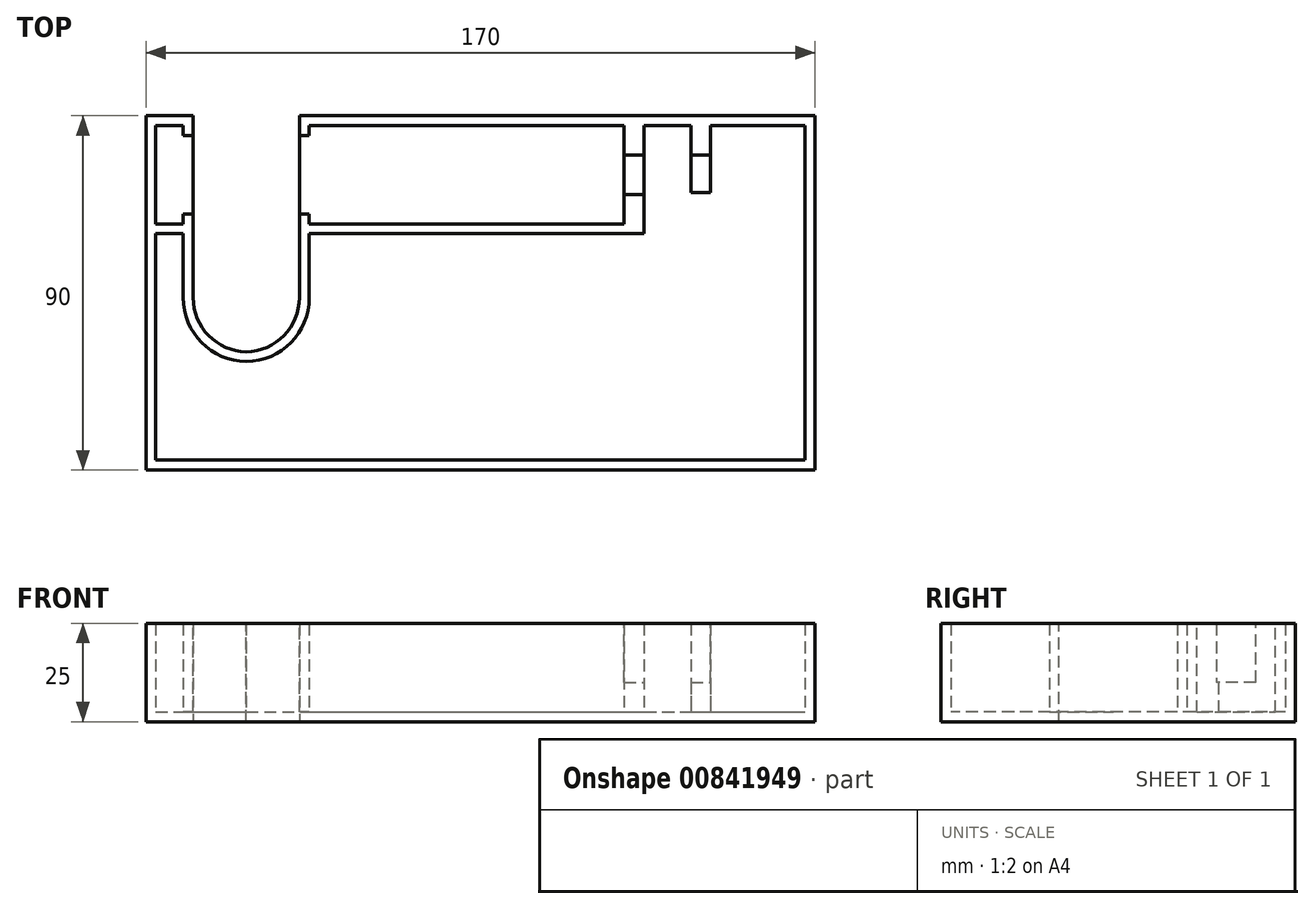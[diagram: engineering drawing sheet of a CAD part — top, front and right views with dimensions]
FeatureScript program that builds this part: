
annotation { "Feature Type Name" : "Feature", "Feature Type Description" : "" }
export const myFeature = defineFeature(function(context is Context, id is Id, definition is map)
    precondition{}
    {
        {
            var Q0;
            Q0=qCreatedBy(makeId("Top.planeOp"),FACE);
            var sketch = newSketch(context, id + "F0", { "sketchPlane" : qUnion([Q0])});
            skLineSegment(sketch, "E0.bottom", {"start": v(-85, 45) * mm, "end": v(85, 45) * mm});
            skLineSegment(sketch, "E0.top", {"start": v(-85, -45) * mm, "end": v(85, -45) * mm});
            skLineSegment(sketch, "E0.left", {"start": v(-85, 45) * mm, "end": v(-85, -45) * mm});
            skLineSegment(sketch, "E0.right", {"start": v(85, 45) * mm, "end": v(85, -45) * mm});
            skPoint(sketch, "E0.middle", {"position": v(0, 0) * mm});
            skLineSegment(sketch, "E1.bottom", {"start": v(-73, 45) * mm, "end": v(-46, 45) * mm});
            skLineSegment(sketch, "E1.top", {"start": v(-73, -15) * mm, "end": v(-46, -15) * mm});
            skLineSegment(sketch, "E1.left", {"start": v(-73, 45) * mm, "end": v(-73, -15) * mm});
            skLineSegment(sketch, "E1.right", {"start": v(-46, 45) * mm, "end": v(-46, -15) * mm});
            skSolve(sketch);
        }
        {
            var Q0;
            Q0=makeQuery(id+"F0.imprint","IMPRINT",FACE,{"disambiguationData":[TD([[makeQuery(id+"F0.imprint","IMPRINT",EDGE,{"derivedFrom":sQuery(id+"F0.wireOp",EDGE,"E0.top")}),1.0]])]});
            extrude(context, id + "F1", {"entities" : qUnion([Q0]), "depth" : 25 * mm, "offsetDistance" : 25 * mm});
        }
        {
            var Q0;
            Q0=makeQuery(id+"F1.opExtrude","SWEPT_EDGE",EDGE,{"disambiguationData":[OSD([sQuery(id+"F0.wireOp",EDGE,"E1.top"),sQuery(id+"F0.wireOp",EDGE,"E1.left")])]});
            var Q1;
            Q1=makeQuery(id+"F1.opExtrude","SWEPT_EDGE",EDGE,{"disambiguationData":[OSD([sQuery(id+"F0.wireOp",EDGE,"E1.top"),sQuery(id+"F0.wireOp",EDGE,"E1.right")])]});
            fillet(context, id + "F2", {"entities" : qUnion([Q0, Q1]), "radius" : (27.5 / 2) * mm, "tangentPropagation" : true, "allowEdgeOverflow" : false});
        }
        {
            var Q0;
            Q0=makeQuery(id+"F1.opExtrude","CAP_FACE",FACE,{"disambiguationData":[OSD([sQuery(id+"F0.wireOp",EDGE,"E0.bottom"),sQuery(id+"F0.wireOp",EDGE,"E0.top"),sQuery(id+"F0.wireOp",EDGE,"E0.left"),sQuery(id+"F0.wireOp",EDGE,"E0.right"),sQuery(id+"F0.wireOp",EDGE,"E1.top"),sQuery(id+"F0.wireOp",EDGE,"E1.left"),sQuery(id+"F0.wireOp",EDGE,"E1.right")])],"isStart":false});
            shell(context, id + "F3", {"entities" : qUnion([Q0]), "thickness" : 2.5 * mm});
        }
        {
            var Q0;
            Q0=makeQuery(id+"F1.opExtrude","CAP_FACE",FACE,{"disambiguationData":[OSD([sQuery(id+"F0.wireOp",EDGE,"E0.bottom"),sQuery(id+"F0.wireOp",EDGE,"E0.top"),sQuery(id+"F0.wireOp",EDGE,"E0.left"),sQuery(id+"F0.wireOp",EDGE,"E0.right"),sQuery(id+"F0.wireOp",EDGE,"E1.top"),sQuery(id+"F0.wireOp",EDGE,"E1.left"),sQuery(id+"F0.wireOp",EDGE,"E1.right")])],"isStart":false});
            var sketch = newSketch(context, id + "F4", { "sketchPlane" : qUnion([Q0])});
            skLineSegment(sketch, "E2.bottom", {"start": v(-75.5, 40) * mm, "end": v(-43.5, 40) * mm});
            skLineSegment(sketch, "E2.top", {"start": v(-75.5, 20) * mm, "end": v(-43.5, 20) * mm});
            skLineSegment(sketch, "E2.left", {"start": v(-75.5, 40) * mm, "end": v(-75.5, 20) * mm});
            skLineSegment(sketch, "E2.right", {"start": v(-43.5, 40) * mm, "end": v(-43.5, 20) * mm});
            skSolve(sketch);
        }
        {
            var Q0;
            {var subQ0=sQuery(id+"F4.wireOp",EDGE,"E2.left");Q0=makeQuery(id+"F4.imprint","IMPRINT",FACE,{"disambiguationData":[TD([[makeQuery(id+"F4.imprint","IMPRINT",EDGE,{"derivedFrom":subQ0}),1.0]])]});}
            var Q1;
            {var subQ0=sQuery(id+"F4.wireOp",EDGE,"E2.right");Q1=makeQuery(id+"F4.imprint","IMPRINT",FACE,{"disambiguationData":[TD([[makeQuery(id+"F4.imprint","IMPRINT",EDGE,{"derivedFrom":subQ0}),-1.0]])]});}
            var Q2;
            Q2=makeQuery(id+"F3.opShell","OFFSET_FACE",FACE,{"disambiguationData":[OSD([sQuery(id+"F0.wireOp",EDGE,"E0.bottom"),sQuery(id+"F0.wireOp",EDGE,"E0.top"),sQuery(id+"F0.wireOp",EDGE,"E0.left"),sQuery(id+"F0.wireOp",EDGE,"E0.right"),sQuery(id+"F0.wireOp",EDGE,"E1.top"),sQuery(id+"F0.wireOp",EDGE,"E1.left"),sQuery(id+"F0.wireOp",EDGE,"E1.right")])]});
            extrude(context, id + "F5", {"entities" : qUnion([Q0, Q1]), "operationType" : NewBodyOperationType.REMOVE, "endBound" : BoundingType.UP_TO_SURFACE, "oppositeDirection" : true, "depth" : 25 * mm, "endBoundEntityFace" : qUnion([Q2]), "offsetDistance" : 25 * mm});
        }
        {
            var Q0;
            {var subQ0=sQuery(id+"F0.wireOp",EDGE,"E1.right");var subQ1=sQuery(id+"F0.wireOp",EDGE,"E1.left");var subQ2=sQuery(id+"F0.wireOp",EDGE,"E1.top");var subQ3=sQuery(id+"F0.wireOp",EDGE,"E0.right");var subQ4=sQuery(id+"F0.wireOp",EDGE,"E0.left");var subQ5=sQuery(id+"F0.wireOp",EDGE,"E0.top");var subQ6=sQuery(id+"F0.wireOp",EDGE,"E0.bottom");Q0=makeQuery(id+"F5.boolean.opBoolean","MERGE",FACE,{"derivedFrom":[makeQuery(id+"F3.opShell","OFFSET_FACE",FACE,{"disambiguationData":[OSD([subQ6,subQ5,subQ4,subQ3,subQ2,subQ1,subQ0])]}),makeQuery(id+"F5.opExtrude","CAP_FACE",FACE,{"disambiguationData":[OSD([subQ6,subQ5,subQ4,subQ3,subQ2,subQ1,subQ0]),OD(0.0)],"isStart":false}),makeQuery(id+"F5.opExtrude","CAP_FACE",FACE,{"disambiguationData":[OSD([subQ6,subQ5,subQ4,subQ3,subQ2,subQ1,subQ0]),OD(1.0)],"isStart":false})]});}
            var sketch = newSketch(context, id + "F6", { "sketchPlane" : qUnion([Q0])});
            skLineSegment(sketch, "E3.bottom", {"start": v(36.5, 42.5) * mm, "end": v(41.5, 42.5) * mm});
            skLineSegment(sketch, "E3.top", {"start": v(36.5, 17.5) * mm, "end": v(41.5, 17.5) * mm});
            skLineSegment(sketch, "E3.left", {"start": v(36.5, 42.5) * mm, "end": v(36.5, 17.5) * mm});
            skLineSegment(sketch, "E3.right", {"start": v(41.5, 42.5) * mm, "end": v(41.5, 17.5) * mm});
            skLineSegment(sketch, "E4.bottom", {"start": v(53.5, 42.5) * mm, "end": v(58.5, 42.5) * mm});
            skLineSegment(sketch, "E4.top", {"start": v(53.5, 25.5) * mm, "end": v(58.5, 25.5) * mm});
            skLineSegment(sketch, "E4.left", {"start": v(53.5, 42.5) * mm, "end": v(53.5, 25.5) * mm});
            skLineSegment(sketch, "E4.right", {"start": v(58.5, 42.5) * mm, "end": v(58.5, 25.5) * mm});
            skSolve(sketch);
        }
        {
            var Q0;
            Q0 = qSketchRegion(id + "F6", true);
            var Q1;
            {var subQ0=sQuery(id+"F0.wireOp",EDGE,"E0.top");var subQ1=sQuery(id+"F0.wireOp",EDGE,"E0.right");var subQ2=sQuery(id+"F0.wireOp",EDGE,"E0.bottom");var subQ3=sQuery(id+"F0.wireOp",EDGE,"E1.right");var subQ6=sQuery(id+"F0.wireOp",EDGE,"E0.left");var subQ7=sQuery(id+"F0.wireOp",EDGE,"E1.left");Q1=makeQuery(id+"F5.boolean.opBoolean","SPLIT",FACE,{"disambiguationData":[TD([makeQuery(id+"F1.opExtrude","SWEPT_FACE",FACE,{"disambiguationData":[OSD([subQ0])]})])],"derivedFrom":makeQuery(id+"F1.opExtrude","CAP_FACE",FACE,{"disambiguationData":[OSD([subQ2,subQ0,subQ6,subQ1,sQuery(id+"F0.wireOp",EDGE,"E1.top"),subQ7,subQ3])],"isStart":false})});}
            extrude(context, id + "F7", {"entities" : qUnion([Q0]), "operationType" : NewBodyOperationType.ADD, "endBound" : BoundingType.UP_TO_SURFACE, "depth" : 25 * mm, "endBoundEntityFace" : qUnion([Q1]), "offsetDistance" : 25 * mm});
        }
        {
            var Q0;
            {var subQ0=sQuery(id+"F0.wireOp",EDGE,"E1.right");var subQ1=sQuery(id+"F0.wireOp",EDGE,"E1.left");var subQ2=sQuery(id+"F0.wireOp",EDGE,"E1.top");var subQ3=sQuery(id+"F0.wireOp",EDGE,"E0.right");var subQ4=sQuery(id+"F0.wireOp",EDGE,"E0.left");var subQ5=sQuery(id+"F0.wireOp",EDGE,"E0.top");var subQ6=sQuery(id+"F0.wireOp",EDGE,"E0.bottom");Q0=makeQuery(id+"F5.boolean.opBoolean","MERGE",FACE,{"derivedFrom":[makeQuery(id+"F3.opShell","OFFSET_FACE",FACE,{"disambiguationData":[OSD([subQ6,subQ5,subQ4,subQ3,subQ2,subQ1,subQ0])]}),makeQuery(id+"F5.opExtrude","CAP_FACE",FACE,{"disambiguationData":[OSD([subQ6,subQ5,subQ4,subQ3,subQ2,subQ1,subQ0]),OD(0.0)],"isStart":false}),makeQuery(id+"F5.opExtrude","CAP_FACE",FACE,{"disambiguationData":[OSD([subQ6,subQ5,subQ4,subQ3,subQ2,subQ1,subQ0]),OD(1.0)],"isStart":false})]});}
            var sketch = newSketch(context, id + "F8", { "sketchPlane" : qUnion([Q0])});
            skLineSegment(sketch, "E5.bottom", {"start": v(-82.5, 17.5) * mm, "end": v(41.5, 17.5) * mm});
            skLineSegment(sketch, "E5.top", {"start": v(-82.5, 15) * mm, "end": v(41.5, 15) * mm});
            skLineSegment(sketch, "E5.left", {"start": v(-82.5, 17.5) * mm, "end": v(-82.5, 15) * mm});
            skLineSegment(sketch, "E5.right", {"start": v(41.5, 17.5) * mm, "end": v(41.5, 15) * mm});
            skSolve(sketch);
        }
        {
            var Q0;
            {var subQ0=sQuery(id+"F8.wireOp",EDGE,"E5.left");Q0=makeQuery(id+"F8.imprint","IMPRINT",FACE,{"disambiguationData":[TD([[makeQuery(id+"F8.imprint","IMPRINT",EDGE,{"derivedFrom":subQ0}),1.0]])]});}
            var Q1;
            {var subQ0=sQuery(id+"F8.wireOp",EDGE,"E5.right");Q1=makeQuery(id+"F8.imprint","IMPRINT",FACE,{"disambiguationData":[TD([[makeQuery(id+"F8.imprint","IMPRINT",EDGE,{"derivedFrom":subQ0}),-1.0]])]});}
            var Q2;
            {var subQ0=sQuery(id+"F0.wireOp",EDGE,"E0.top");var subQ1=sQuery(id+"F0.wireOp",EDGE,"E0.right");var subQ2=sQuery(id+"F0.wireOp",EDGE,"E0.bottom");var subQ3=sQuery(id+"F0.wireOp",EDGE,"E1.right");var subQ6=sQuery(id+"F0.wireOp",EDGE,"E0.left");var subQ7=sQuery(id+"F0.wireOp",EDGE,"E1.left");Q2=makeQuery(id+"F7.boolean.opBoolean","MERGE",FACE,{"derivedFrom":[makeQuery(id+"F5.boolean.opBoolean","SPLIT",FACE,{"disambiguationData":[TD([makeQuery(id+"F1.opExtrude","SWEPT_FACE",FACE,{"disambiguationData":[OSD([subQ0])]})])],"derivedFrom":makeQuery(id+"F1.opExtrude","CAP_FACE",FACE,{"disambiguationData":[OSD([subQ2,subQ0,subQ6,subQ1,sQuery(id+"F0.wireOp",EDGE,"E1.top"),subQ7,subQ3])],"isStart":false})}),makeQuery(id+"F7.opExtrude","CAP_FACE",FACE,{"disambiguationData":[OSD([sQuery(id+"F6.wireOp",EDGE,"E3.bottom"),sQuery(id+"F6.wireOp",EDGE,"E3.top"),sQuery(id+"F6.wireOp",EDGE,"E3.left"),sQuery(id+"F6.wireOp",EDGE,"E3.right")])],"isStart":false})]});}
            extrude(context, id + "F9", {"entities" : qUnion([Q0, Q1]), "operationType" : NewBodyOperationType.ADD, "endBound" : BoundingType.UP_TO_SURFACE, "depth" : 25 * mm, "endBoundEntityFace" : qUnion([Q2]), "offsetDistance" : 25 * mm});
        }
        {
            var Q0;
            {var subQ0=sQuery(id+"F8.wireOp",EDGE,"E5.top");var subQ1=sQuery(id+"F8.wireOp",EDGE,"E5.bottom");var subQ2=sQuery(id+"F0.wireOp",EDGE,"E1.right");var subQ3=sQuery(id+"F0.wireOp",EDGE,"E1.left");var subQ4=sQuery(id+"F0.wireOp",EDGE,"E0.top");var subQ5=sQuery(id+"F0.wireOp",EDGE,"E0.right");var subQ6=sQuery(id+"F0.wireOp",EDGE,"E0.bottom");var subQ10=sQuery(id+"F0.wireOp",EDGE,"E0.left");var subQ22=sQuery(id+"F0.wireOp",EDGE,"E1.top");var subQ23=makeQuery(id+"F1.opExtrude","CAP_FACE",FACE,{"disambiguationData":[OSD([subQ6,subQ4,subQ10,subQ5,subQ22,subQ3,subQ2])],"isStart":false});Q0=makeQuery(id+"F9.boolean.opBoolean","MERGE",FACE,{"derivedFrom":[makeQuery(id+"F5.boolean.opBoolean","SPLIT",FACE,{"disambiguationData":[TD([makeQuery(id+"F2.opFillet","BLEND_FACE",FACE,{"disambiguationData":[OSD([subQ22,subQ3])]})])],"derivedFrom":subQ23}),makeQuery(id+"F7.boolean.opBoolean","MERGE",FACE,{"derivedFrom":[makeQuery(id+"F5.boolean.opBoolean","SPLIT",FACE,{"disambiguationData":[TD([makeQuery(id+"F1.opExtrude","SWEPT_FACE",FACE,{"disambiguationData":[OSD([subQ4])]})])],"derivedFrom":subQ23}),makeQuery(id+"F7.opExtrude","CAP_FACE",FACE,{"disambiguationData":[OSD([sQuery(id+"F6.wireOp",EDGE,"E3.bottom"),sQuery(id+"F6.wireOp",EDGE,"E3.top"),sQuery(id+"F6.wireOp",EDGE,"E3.left"),sQuery(id+"F6.wireOp",EDGE,"E3.right")])],"isStart":false}),makeQuery(id+"F7.opExtrude","CAP_FACE",FACE,{"disambiguationData":[OSD([sQuery(id+"F6.wireOp",EDGE,"E4.bottom"),sQuery(id+"F6.wireOp",EDGE,"E4.top"),sQuery(id+"F6.wireOp",EDGE,"E4.left"),sQuery(id+"F6.wireOp",EDGE,"E4.right")])],"isStart":false})]}),makeQuery(id+"F9.opExtrude","CAP_FACE",FACE,{"disambiguationData":[OSD([subQ3,subQ1,subQ0,sQuery(id+"F8.wireOp",EDGE,"E5.left")])],"isStart":false}),makeQuery(id+"F9.opExtrude","CAP_FACE",FACE,{"disambiguationData":[OSD([subQ2,subQ1,subQ0,sQuery(id+"F8.wireOp",EDGE,"E5.right")])],"isStart":false})]});}
            var sketch = newSketch(context, id + "F10", { "sketchPlane" : qUnion([Q0])});
            skLineSegment(sketch, "E6.bottom", {"start": v(36.5, 35) * mm, "end": v(58.5, 35) * mm});
            skLineSegment(sketch, "E6.top", {"start": v(36.5, 25) * mm, "end": v(58.5, 25) * mm});
            skLineSegment(sketch, "E6.left", {"start": v(36.5, 35) * mm, "end": v(36.5, 25) * mm});
            skLineSegment(sketch, "E6.right", {"start": v(58.5, 35) * mm, "end": v(58.5, 25) * mm});
            skSolve(sketch);
        }
        {
            var Q0;
            Q0 = qSketchRegion(id + "F10", true);
            extrude(context, id + "F11", {"entities" : qUnion([Q0]), "operationType" : NewBodyOperationType.REMOVE, "oppositeDirection" : true, "depth" : 15 * mm, "offsetDistance" : 25 * mm});
        }
    });
